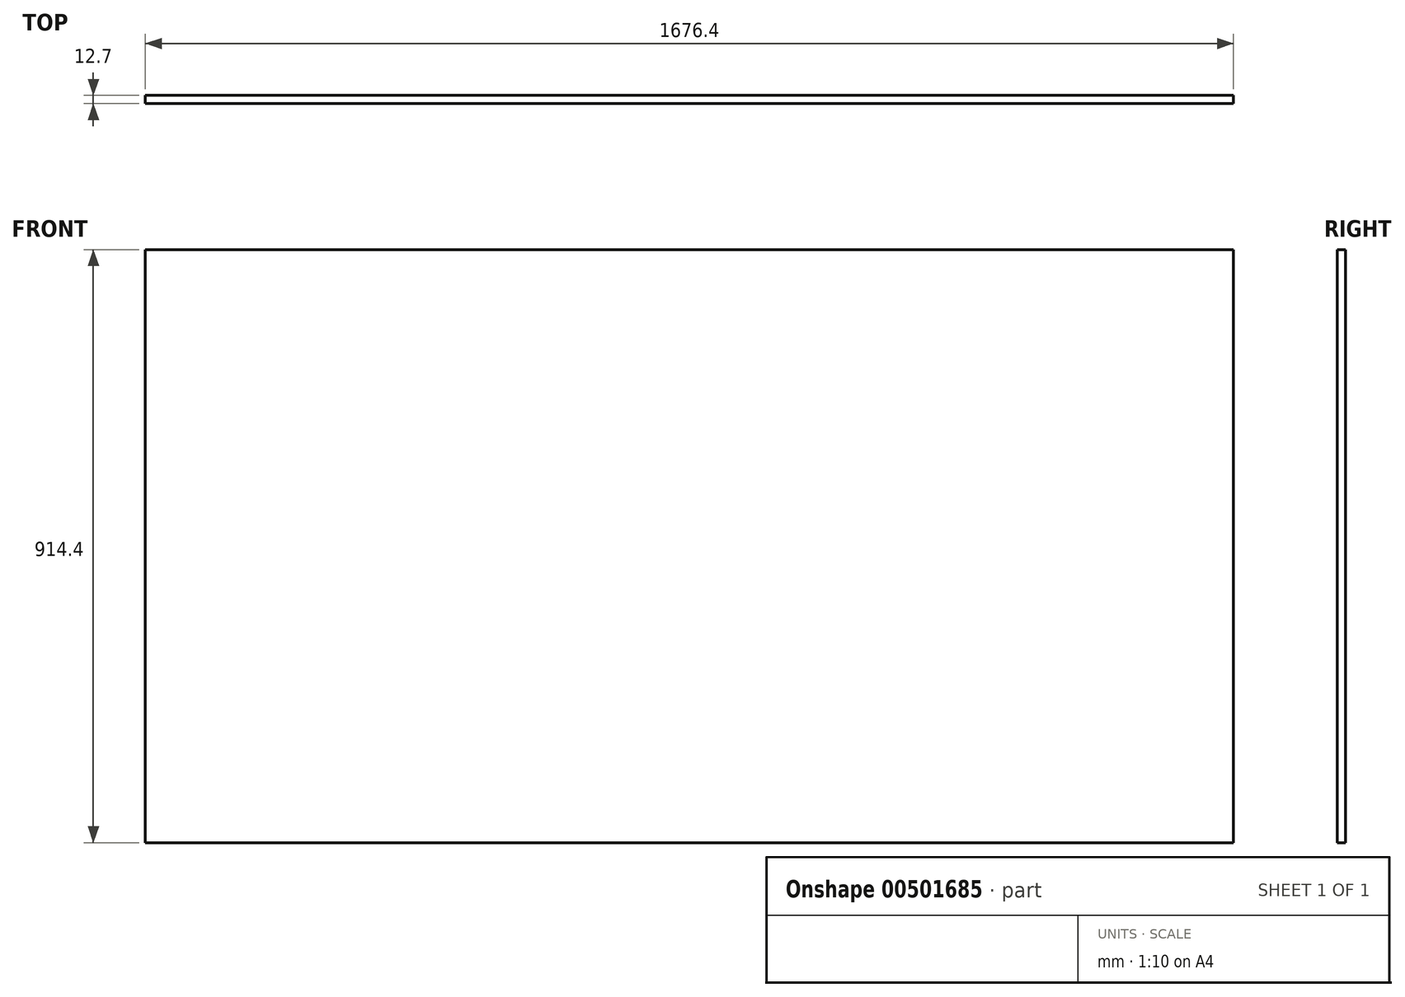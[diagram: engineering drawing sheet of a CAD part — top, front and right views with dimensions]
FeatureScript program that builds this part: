
annotation { "Feature Type Name" : "Feature", "Feature Type Description" : "" }
export const myFeature = defineFeature(function(context is Context, id is Id, definition is map)
    precondition{}
    {
        {
            var Q0;
            Q0=qCreatedBy(makeId("Front.planeOp"),FACE);
            var sketch = newSketch(context, id + "F0", { "sketchPlane" : qUnion([Q0])});
            skLineSegment(sketch, "E0.bottom", {"start": v(838.2, 424.76) * mm, "end": v(-838.2, 424.76) * mm});
            skLineSegment(sketch, "E0.top", {"start": v(838.2, -489.64) * mm, "end": v(-838.2, -489.64) * mm});
            skLineSegment(sketch, "E0.left", {"start": v(838.2, 424.76) * mm, "end": v(838.2, -489.64) * mm});
            skLineSegment(sketch, "E0.right", {"start": v(-838.2, 424.76) * mm, "end": v(-838.2, -489.64) * mm});
            skPoint(sketch, "E0.middle", {"position": v(0, -32.44) * mm});
            skSolve(sketch);
        }
        {
            var Q0;
            Q0=makeQuery(id+"F0.imprint","IMPRINT",FACE,{"disambiguationData":[TD([[makeQuery(id+"F0.imprint","IMPRINT",EDGE,{"derivedFrom":sQuery(id+"F0.wireOp",EDGE,"E0.bottom")}),1.0]])]});
            extrude(context, id + "F1", {"entities" : qUnion([Q0]), "depth" : 12.7 * mm});
        }
    });
